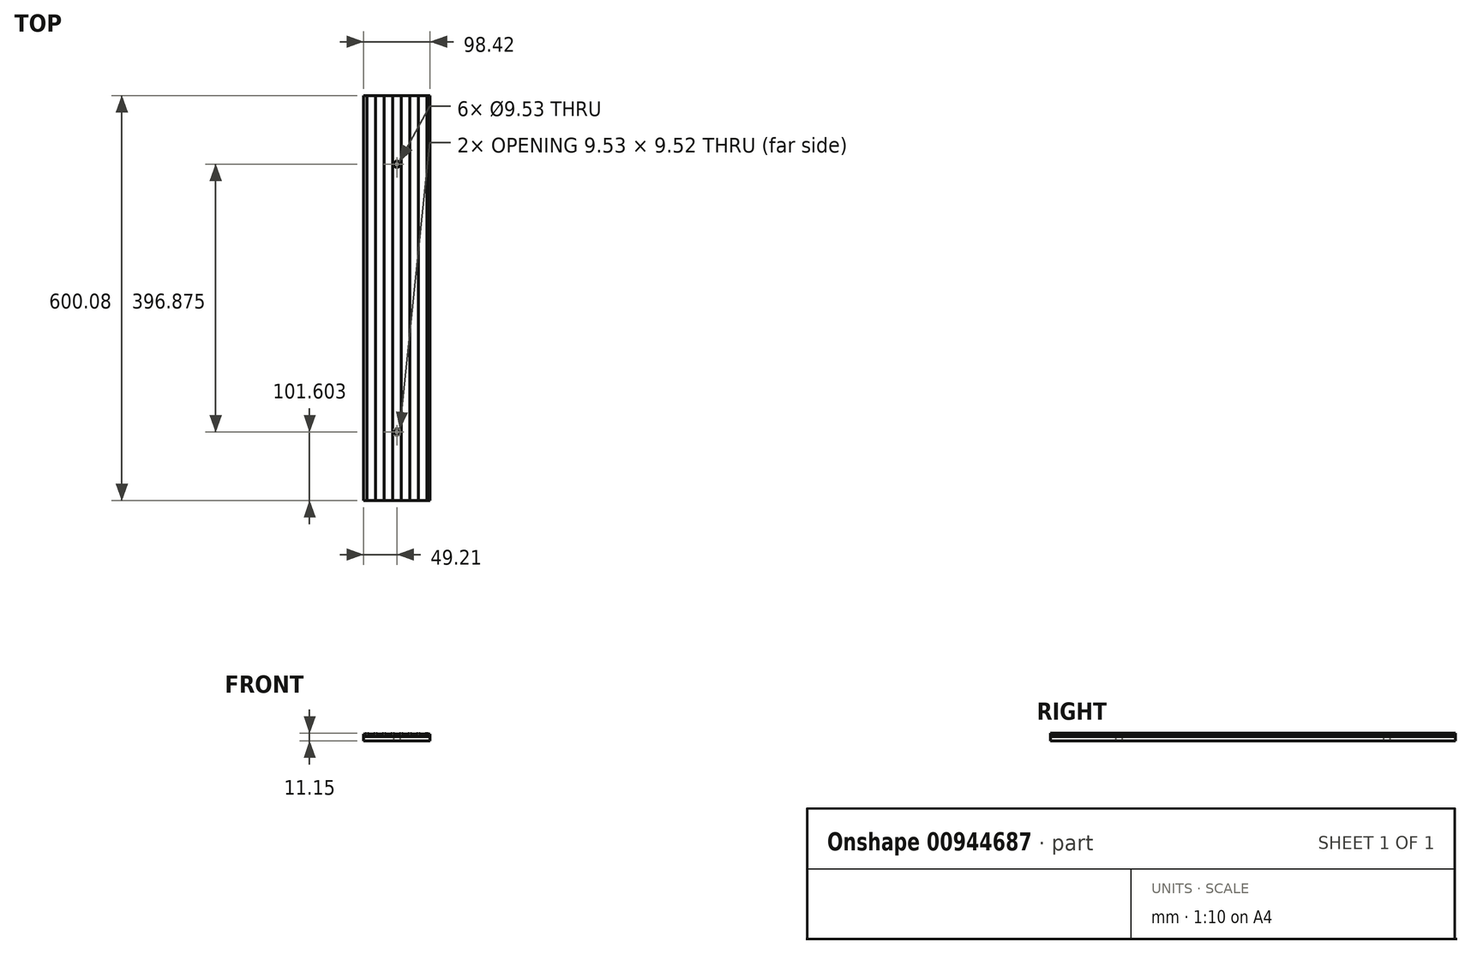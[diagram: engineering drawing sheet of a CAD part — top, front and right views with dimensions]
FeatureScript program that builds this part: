
annotation { "Feature Type Name" : "Feature", "Feature Type Description" : "" }
export const myFeature = defineFeature(function(context is Context, id is Id, definition is map)
    precondition{}
    {
        {
            var Q0;
            Q0=qCreatedBy(makeId("Front.planeOp"),FACE);
            var sketch = newSketch(context, id + "F0", { "sketchPlane" : qUnion([Q0])});
            skLineSegment(sketch, "E0.bottom", {"start": v(49.21, 0) * mm, "end": v(0, 0) * mm});
            skLineSegment(sketch, "E0.top", {"start": v(49.21, 6) * mm, "end": v(0, 6) * mm});
            skLineSegment(sketch, "E0.left", {"start": v(49.21, 0) * mm, "end": v(49.21, 6) * mm});
            skLineSegment(sketch, "E1.top", {"start": v(49.21, 7.08) * mm, "end": v(0, 7.08) * mm});
            skLineSegment(sketch, "E1.left", {"start": v(49.21, 6) * mm, "end": v(49.21, 7.08) * mm});
            skLineSegment(sketch, "E2", {"start": v(49.21, 7.08) * mm, "end": v(49.21, 11.15) * mm});
            skArc(sketch, "E3.2.0.0", {"start": v(49.21, 10.04) * mm, "mid": v(46.8, 10.42) * mm, "end": v(44.45, 11.15) * mm});
            skArc(sketch, "E3.3.0.0", {"start": v(44.45, 11.15) * mm, "mid": v(38.1, 9.96) * mm, "end": v(31.75, 11.15) * mm});
            skArc(sketch, "E3.4.0.0", {"start": v(31.75, 11.15) * mm, "mid": v(25.4, 9.96) * mm, "end": v(19.05, 11.15) * mm});
            skArc(sketch, "E3.5.0.0", {"start": v(19.05, 11.15) * mm, "mid": v(12.7, 9.96) * mm, "end": v(6.35, 11.15) * mm});
            skArc(sketch, "E3.6.0.0", {"start": v(6.35, 11.15) * mm, "mid": v(3.23, 10.26) * mm, "end": v(0, 9.96) * mm});
            skLineSegment(sketch, "E3.direction1", {"start": v(-105.06, -36.9) * mm, "end": v(-92.36, -36.9) * mm, "construction": true});
            skPoint(sketch, "E4.orphan", {"position": v(-93.66, 11.07) * mm});
            skLineSegment(sketch, "E5", {"start": v(0, 0) * mm, "end": v(0, 9.96) * mm, "construction": true});
            skLineSegment(sketch, "E6.trimOffspring", {"start": v(0, 27.6) * mm, "end": v(0, 43.35) * mm, "construction": true});
            skLineSegment(sketch, "E7", {"start": v(19.05, 11.15) * mm, "end": v(19.05, 7.08) * mm, "construction": true});
            skLineSegment(sketch, "E8", {"start": v(6.35, 11.15) * mm, "end": v(44.45, 11.15) * mm, "construction": true});
            skLineSegment(sketch, "E9.MirrorCS", {"start": v(-49.21, 6) * mm, "end": v(-49.21, 7.08) * mm});
            skLineSegment(sketch, "E10.MirrorCS", {"start": v(-49.21, 6) * mm, "end": v(0, 6) * mm});
            skLineSegment(sketch, "E11.MirrorCS", {"start": v(-49.21, 7.08) * mm, "end": v(-49.21, 11.15) * mm});
            skLineSegment(sketch, "E12.MirrorCS", {"start": v(-19.05, 11.15) * mm, "end": v(-19.05, 7.08) * mm, "construction": true});
            skLineSegment(sketch, "E13.MirrorCS", {"start": v(-49.21, 7.08) * mm, "end": v(0, 7.08) * mm});
            skLineSegment(sketch, "E14.MirrorCS", {"start": v(-49.21, 0) * mm, "end": v(0, 0) * mm});
            skArc(sketch, "E15.MirrorCS", {"start": v(-19.05, 11.15) * mm, "mid": v(-12.7, 9.96) * mm, "end": v(-6.35, 11.15) * mm});
            skLineSegment(sketch, "E16.MirrorCS", {"start": v(-6.35, 11.15) * mm, "end": v(-44.45, 11.15) * mm, "construction": true});
            skArc(sketch, "E17.MirrorCS", {"start": v(-49.21, 10.04) * mm, "mid": v(-46.8, 10.42) * mm, "end": v(-44.45, 11.15) * mm});
            skArc(sketch, "E18.MirrorCS", {"start": v(-31.75, 11.15) * mm, "mid": v(-25.4, 9.96) * mm, "end": v(-19.05, 11.15) * mm});
            skLineSegment(sketch, "E19.MirrorCS", {"start": v(-49.21, 0) * mm, "end": v(-49.21, 6) * mm});
            skArc(sketch, "E20.MirrorCS", {"start": v(-44.45, 11.15) * mm, "mid": v(-38.1, 9.96) * mm, "end": v(-31.75, 11.15) * mm});
            skArc(sketch, "E21.MirrorCS", {"start": v(-6.35, 11.15) * mm, "mid": v(-3.23, 10.26) * mm, "end": v(0, 9.96) * mm});
            skPoint(sketch, "E22.orphan", {"position": v(51.6, 9.98) * mm});
            skPoint(sketch, "E23.orphan", {"position": v(-51.6, 9.98) * mm});
            skSolve(sketch);
        }
        {
            var Q0;
            Q0=makeQuery(id+"F0.imprint","IMPRINT",FACE,{"disambiguationData":[TD([[makeQuery(id+"F0.imprint","IMPRINT",EDGE,{"derivedFrom":sQuery(id+"F0.wireOp",EDGE,"E0.bottom")}),-1.0]])]});
            var Q1;
            Q1=sQuery(id+"F0.wireOp",EDGE,"E0.left");
            var Q2;
            Q2=sQuery(id+"F0.wireOp",EDGE,"E0.bottom");
            var Q3;
            Q3=sQuery(id+"F0.wireOp",EDGE,"E0.top");
            var Q4;
            Q4=sQuery(id+"F0.wireOp",EDGE,"E0.right");
            extrude(context, id + "F1", {"entities" : qUnion([Q0]), "surfaceEntities" : qUnion([Q1, Q2, Q3, Q4]), "endBound" : BoundingType.SYMMETRIC, "depth" : 600.07 * mm, "offsetDistance" : 25.4 * mm});
        }
        {
            var Q0;
            Q0=makeQuery(id+"F0.imprint","IMPRINT",FACE,{"disambiguationData":[TD([[makeQuery(id+"F0.imprint","IMPRINT",EDGE,{"derivedFrom":sQuery(id+"F0.wireOp",EDGE,"E0.top")}),-1.0]])]});
            extrude(context, id + "F2", {"entities" : qUnion([Q0]), "endBound" : BoundingType.SYMMETRIC, "depth" : 600.07 * mm, "offsetDistance" : 25.4 * mm});
        }
        {
            var Q0;
            {var subQ3=sQuery(id+"F0.wireOp",EDGE,"E1.top");Q0=makeQuery(id+"F0.imprint","IMPRINT",FACE,{"disambiguationData":[TD([[makeQuery(id+"F0.imprint","IMPRINT",EDGE,{"derivedFrom":subQ3}),-1.0]])]});}
            extrude(context, id + "F3", {"entities" : qUnion([Q0]), "endBound" : BoundingType.SYMMETRIC, "depth" : 600.07 * mm, "offsetDistance" : 25.4 * mm});
        }
        {
            var Q0;
            Q0=qCreatedBy(makeId("Top.planeOp"),FACE);
            var sketch = newSketch(context, id + "F4", { "sketchPlane" : qUnion([Q0])});
            skLineSegment(sketch, "E24", {"start": v(0, 749.3) * mm, "end": v(0, -749.3) * mm, "construction": true});
            skPoint(sketch, "E25", {"position": v(0, 0) * mm});
            skCircle(sketch, "E26", {"center": v(0, 198.44) * mm, "radius": 4.76 * mm});
            skLineSegment(sketch, "E27", {"start": v(0, 0) * mm, "end": v(-13.94, 0) * mm, "construction": true});
            skCircle(sketch, "E28.MirrorC", {"center": v(0, -198.44) * mm, "radius": 4.76 * mm});
            skSolve(sketch);
        }
        {
            var Q0;
            Q0=qSketchRegion(id+"F4",true);
            extrude(context, id + "F5", {"entities" : qUnion([Q0]), "operationType" : NewBodyOperationType.REMOVE, "depth" : 25.4 * mm, "offsetDistance" : 25.4 * mm});
        }
    });
